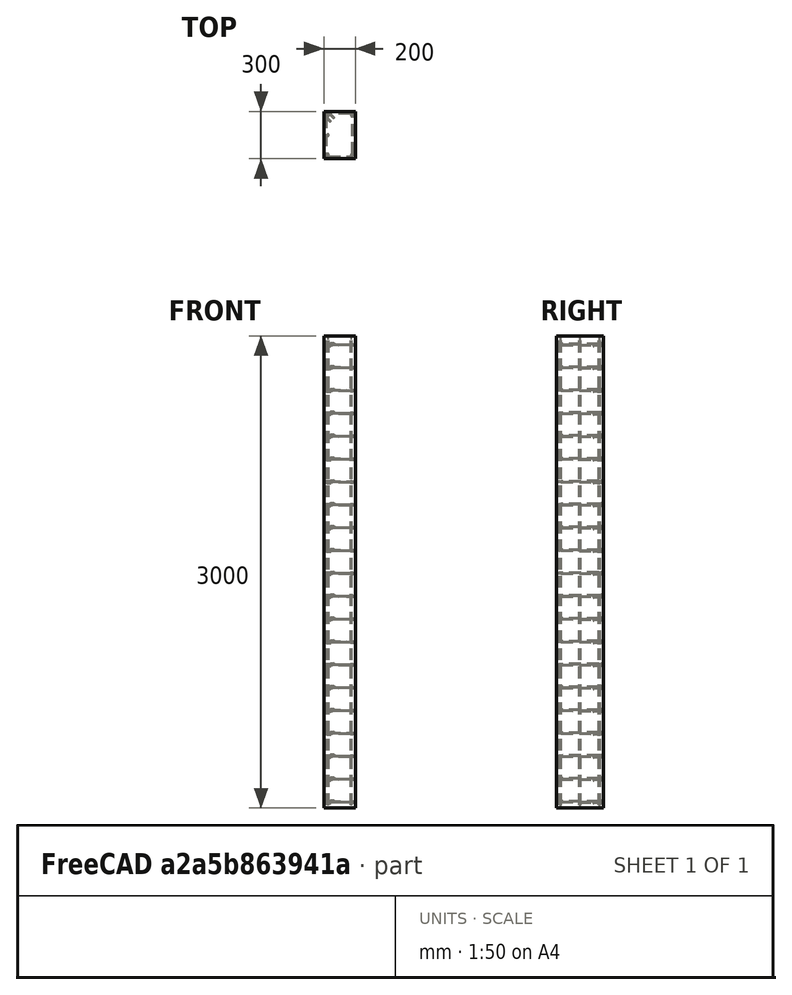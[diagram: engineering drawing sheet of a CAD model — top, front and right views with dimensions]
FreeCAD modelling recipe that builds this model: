
FCSTD DOCUMENT  (FreeCAD 0.21R33771 (Git))
Label: 3D Designe of Rainforced Coloumn 
License: All rights reserved
objects: Part::FeaturePython×4, Sketcher::SketchObject×2, Part::Part2DObjectPython×1
note: 7 computed .brp shape members not serialized (recipe doc carries the construction recipe); baked Part::Feature solids carry a one-line shape summary decoded from their .brp

FEATURE [Part::FeaturePython] Structure  label="Column"  # Arch/BIM 24 (typed FeaturePython)
  BaseMirror = false
  BaseOffsetX = 0
  BaseOffsetY = 0
  BasePerpendicularToTool = false
  BaseRotation = 0
  ComputedLength = 3000
  FaceMaker = 0
  Height = 3000
  HorizontalArea = 60000
  IfcData = attributes={"GlobalId": {"name": "GlobalId", "type": "IfcGloballyUniqueId", "is_enum": false, "enum_values": []}, "Description": {"... (+438 chars omitted),+1 more (map truncated)
  IfcType = 24
  Length = 200
  MoveBase = false
  MoveWithHost = false
  Nodes = (2) [(-7.77156e-16,4.54747e-15,0),(-7.77156e-16,4.54747e-15,3000)]
  NodesOffset = 0
  Normal = (0,0,0)
  PerimeterLength = 1000
  PredefinedType = 0
  ToolOffsetFirst = 0
  ToolOffsetLast = 0
  VerticalArea = 3000000
  Width = 300
FEATURE [Sketcher::SketchObject] Sketch
  FullyConstrained = false
  MapMode = 5
  Placement = pos=(0,-150,0) rot=(1,0,0;1.5708rad)
  Support = -> [Structure]
  sketch-geometry (1):
    g0: LineSegment StartX=-74 StartY=20 StartZ=0 EndX=-74 EndY=2980 EndZ=0
FEATURE [Part::FeaturePython] Rebar  label="StraightRebar"  # Arch/BIM 110 (typed FeaturePython)
  Amount = 3
  AmountCheck = true
  Base = -> Sketch
  Cover = 20
  CoverAlong = Left Side
  Diameter = 12
  Direction = (0,0,0)
  Distance = 0
  FrontCover = 20
  HorizontalArea = 0
  Host = -> Structure
  IfcType = 110
  LeftBottomCover = 20
  Length = 2960
  Mark = StraightRebar
  MoveBase = false
  MoveWithHost = false
  OffsetEnd = 26
  OffsetStart = 26
  Orientation = Vertical
  PerimeterLength = 0
  PlacementList = 3 placements: arithmetic series from (0,26,-5.77316e-15) step (0,124,-2.75335e-14) to (0,274,-6.08402e-14)
  RebarShape = 0
  RightTopCover = 20
  Rounding = 0
  Spacing = 124
  TotalLength = 8880
  TrueSpacing = 3
  VerticalArea = 0
FEATURE [Sketcher::SketchObject] Sketch001
  FullyConstrained = false
  MapMode = 5
  Placement = pos=(0,-150,0) rot=(1,0,0;1.5708rad)
  Support = -> [Structure]
  sketch-geometry (1):
    g0: LineSegment StartX=75 StartY=20 StartZ=0 EndX=75 EndY=2980 EndZ=0
FEATURE [Part::FeaturePython] Rebar001  label="StraightRebar001"  # Arch/BIM 110 (typed FeaturePython)
  Amount = 2
  AmountCheck = true
  Base = -> Sketch001
  Cover = 20
  CoverAlong = Right Side
  Diameter = 10
  Direction = (0,0,0)
  Distance = 0
  FrontCover = 20
  HorizontalArea = 0
  Host = -> Structure
  IfcType = 110
  LeftBottomCover = 20
  Length = 2960
  Mark = StraightRebar001
  MoveBase = false
  MoveWithHost = false
  OffsetEnd = 25
  OffsetStart = 25
  Orientation = Vertical
  PerimeterLength = 0
  PlacementList = 2 placements: [(0,25,-5.55112e-15),(0,275,-6.10623e-14)]
  RebarShape = 0
  RightTopCover = 20
  Rounding = 0
  Spacing = 250
  TotalLength = 5920
  TrueSpacing = 2
  VerticalArea = 0
FEATURE [Part::Part2DObjectPython] Wire  # Draft 2D object (typed FeaturePython)
  Area = 0
  ChamferSize = 0
  Closed = false
  End = (-58.6863,86.0589,-11.331)
  FilletRadius = 0
  Length = 1070.63
  MakeFace = true
  Points = (7) [(-36.0589,108.686,2.2662),(-86,158.627,0),(-86,-136,-2.2662),(84,-136,-4.53241),(84,136,-6.79861),(-108.627,136,-9.06482),(-58.6863,86.0589,-11.331)]
  Start = (-36.0589,108.686,2.2662)
  Subdivisions = 0
  Support = -> [Structure]
FEATURE [Part::FeaturePython] Rebar002  label="Stirrup"  # Arch/BIM 110 (typed FeaturePython)
  Amount = 21
  AmountCheck = false
  Base = -> Wire
  BentAngle = 135
  BentFactor = 4
  BottomCover = 10
  Diameter = 8
  Direction = (0,0,1)
  Distance = 0
  FrontCover = 40
  HorizontalArea = 0
  Host = -> Structure
  IfcType = 110
  LeftCover = 10
  Length = 1070.63
  Mark = Stirrup
  MoveBase = false
  MoveWithHost = false
  OffsetEnd = 44
  OffsetStart = 44
  PerimeterLength = 0
  PlacementList = 21 placements: arithmetic series from (0,0,44) step (0,0,145.2) to (0,0,2948)
  RebarShape = 3
  RightCover = 12
  Rounding = 2
  Spacing = 145.2
  TopCover = 10
  TotalLength = 22483.2
  TrueSpacing = 150
  VerticalArea = 0
